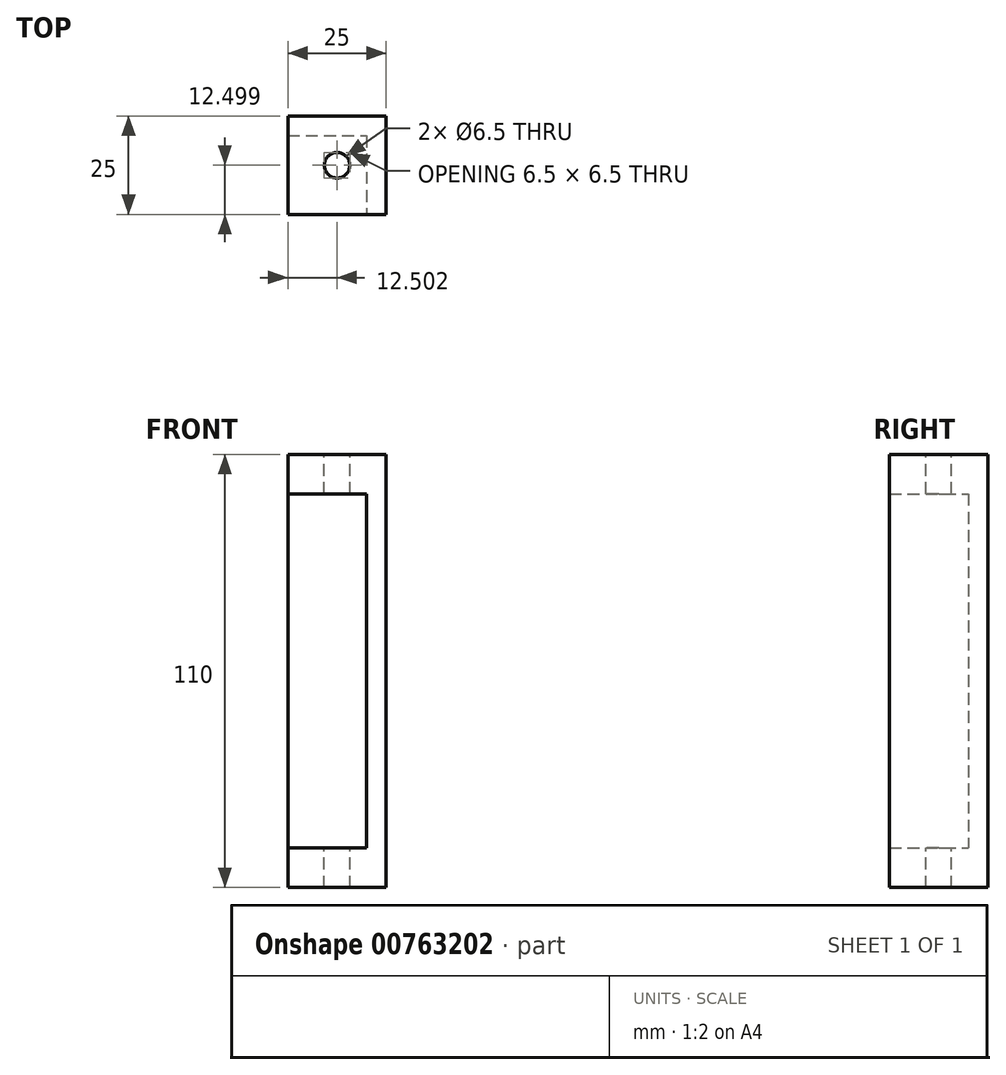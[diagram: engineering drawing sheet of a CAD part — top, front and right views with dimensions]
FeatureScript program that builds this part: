
annotation { "Feature Type Name" : "Feature", "Feature Type Description" : "" }
export const myFeature = defineFeature(function(context is Context, id is Id, definition is map)
    precondition{}
    {
        {
            var Q0;
            Q0=qCreatedBy(makeId("Top.planeOp"),FACE);
            var sketch = newSketch(context, id + "F0", { "sketchPlane" : qUnion([Q0])});
            skLineSegment(sketch, "E0.bottom", {"start": v(-38.35, 32) * mm, "end": v(-13.35, 32) * mm});
            skLineSegment(sketch, "E0.top", {"start": v(-38.35, 7) * mm, "end": v(-13.35, 7) * mm});
            skLineSegment(sketch, "E0.left", {"start": v(-38.35, 32) * mm, "end": v(-38.35, 7) * mm});
            skLineSegment(sketch, "E0.right", {"start": v(-13.35, 32) * mm, "end": v(-13.35, 7) * mm});
            skSolve(sketch);
        }
        {
            var Q0;
            Q0 = qSketchRegion(id + "F0", true);
            extrude(context, id + "F1", {"entities" : qUnion([Q0]), "depth" : 110 * mm, "offsetDistance" : 25 * mm});
        }
        {
            var Q0;
            Q0=makeQuery(id+"F1.opExtrude","SWEPT_FACE",FACE,{"disambiguationData":[OSD([sQuery(id+"F0.wireOp",EDGE,"E0.top")])]});
            var sketch = newSketch(context, id + "F2", { "sketchPlane" : qUnion([Q0])});
            skLineSegment(sketch, "E1.bottom", {"start": v(-45.77, 100) * mm, "end": v(-18.35, 100) * mm});
            skLineSegment(sketch, "E1.top", {"start": v(-45.77, 10) * mm, "end": v(-18.35, 10) * mm});
            skLineSegment(sketch, "E1.left", {"start": v(-45.77, 100) * mm, "end": v(-45.77, 10) * mm});
            skLineSegment(sketch, "E1.right", {"start": v(-18.35, 100) * mm, "end": v(-18.35, 10) * mm});
            skSolve(sketch);
        }
        {
            var Q0;
            Q0 = qSketchRegion(id + "F2", true);
            extrude(context, id + "F3", {"entities" : qUnion([Q0]), "operationType" : NewBodyOperationType.REMOVE, "oppositeDirection" : true, "depth" : 20 * mm, "offsetDistance" : 25 * mm});
        }
        {
            var Q0;
            Q0=makeQuery(id+"F1.opExtrude","CAP_FACE",FACE,{"disambiguationData":[OSD([sQuery(id+"F0.wireOp",EDGE,"E0.bottom"),sQuery(id+"F0.wireOp",EDGE,"E0.top"),sQuery(id+"F0.wireOp",EDGE,"E0.left"),sQuery(id+"F0.wireOp",EDGE,"E0.right")])],"isStart":false});
            var sketch = newSketch(context, id + "F4", { "sketchPlane" : qUnion([Q0])});
            skCircle(sketch, "E2", {"center": v(-25.85, 19.5) * mm, "radius": 3.25 * mm});
            skSolve(sketch);
        }
        {
            var Q0;
            Q0 = qSketchRegion(id + "F4", true);
            extrude(context, id + "F5", {"entities" : qUnion([Q0]), "operationType" : NewBodyOperationType.REMOVE, "endBound" : BoundingType.THROUGH_ALL, "oppositeDirection" : true, "depth" : 25 * mm, "offsetDistance" : 25 * mm});
        }
    });
